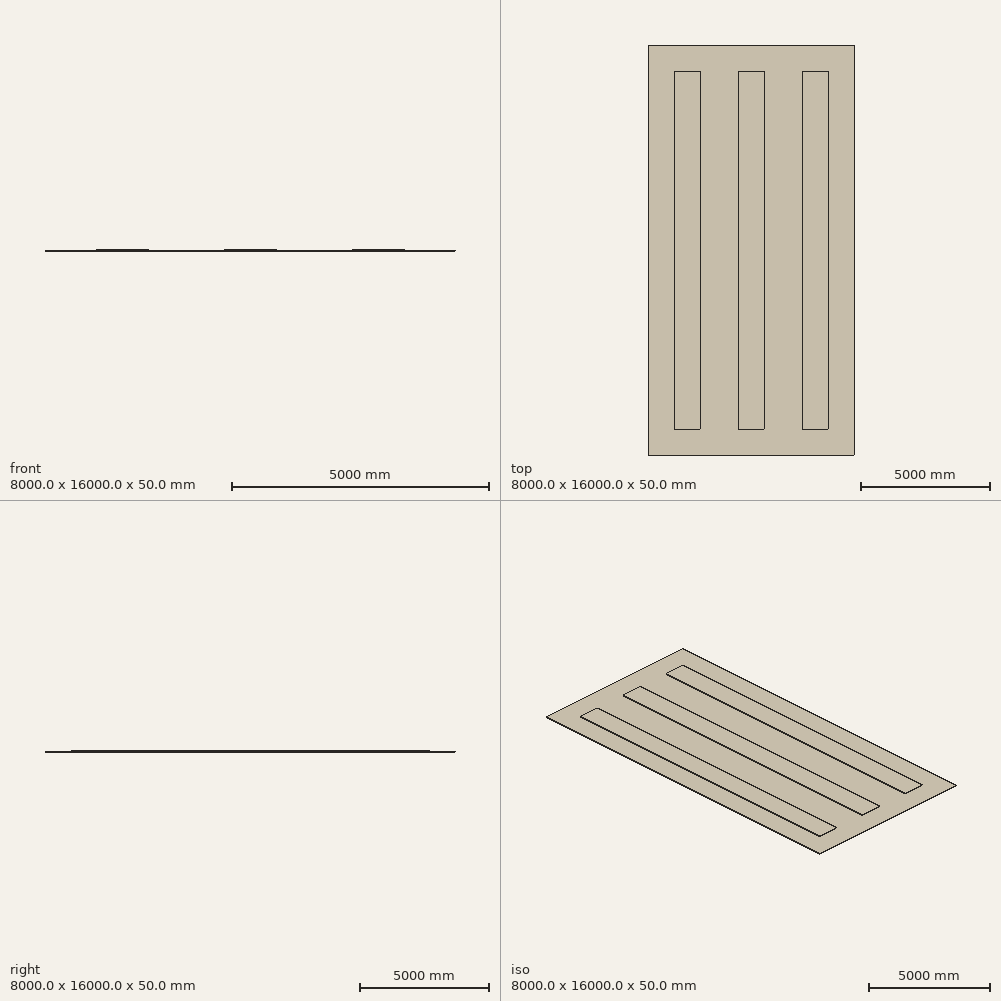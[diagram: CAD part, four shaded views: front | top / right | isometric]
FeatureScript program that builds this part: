
annotation { "Feature Type Name" : "Feature", "Feature Type Description" : "" }
export const myFeature = defineFeature(function(context is Context, id is Id, definition is map)
    precondition{}
    {
        {
            var Q0;
            Q0=qCreatedBy(makeId("Top.planeOp"),FACE);
            var sketch = newSketch(context, id + "F0", { "sketchPlane" : qUnion([Q0])});
            skLineSegment(sketch, "E0.bottom", {"start": v(0, 0) * mm, "end": v(-8000, 0) * mm});
            skLineSegment(sketch, "E0.top", {"start": v(0, 16000) * mm, "end": v(-8000, 16000) * mm});
            skLineSegment(sketch, "E0.left", {"start": v(0, 0) * mm, "end": v(0, 16000) * mm});
            skLineSegment(sketch, "E0.right", {"start": v(-8000, 0) * mm, "end": v(-8000, 16000) * mm});
            skSolve(sketch);
        }
        {
            var Q0;
            Q0=makeQuery(id+"F0.imprint","IMPRINT",FACE,{"disambiguationData":[TD([[makeQuery(id+"F0.imprint","IMPRINT",EDGE,{"derivedFrom":sQuery(id+"F0.wireOp",EDGE,"E0.bottom")}),-1.0]])]});
            extrude(context, id + "F1", {"entities" : qUnion([Q0]), "depth" : 25 * mm, "offsetDistance" : 25 * mm});
        }
        {
            var Q0;
            Q0=makeQuery(id+"F1.opExtrude","CAP_FACE",FACE,{"disambiguationData":[OSD([sQuery(id+"F0.wireOp",EDGE,"E0.bottom"),sQuery(id+"F0.wireOp",EDGE,"E0.top"),sQuery(id+"F0.wireOp",EDGE,"E0.left"),sQuery(id+"F0.wireOp",EDGE,"E0.right")])],"isStart":false});
            var sketch = newSketch(context, id + "F2", { "sketchPlane" : qUnion([Q0])});
            skLineSegment(sketch, "E1", {"start": v(-8000, 0) * mm, "end": v(-7000, 0) * mm});
            skLineSegment(sketch, "E2", {"start": v(-7000, 0) * mm, "end": v(-6000, 0) * mm});
            skLineSegment(sketch, "E3", {"start": v(-6000, 0) * mm, "end": v(-4500, 0) * mm});
            skLineSegment(sketch, "E4", {"start": v(-4500, 0) * mm, "end": v(-3500, 0) * mm});
            skLineSegment(sketch, "E5", {"start": v(-3500, 0) * mm, "end": v(-2000, 0) * mm});
            skLineSegment(sketch, "E6", {"start": v(-2000, 0) * mm, "end": v(-1000, 0) * mm});
            skLineSegment(sketch, "E7", {"start": v(-1000, 0) * mm, "end": v(0, 0) * mm});
            skLineSegment(sketch, "E8", {"start": v(-8000, 0) * mm, "end": v(-8000, 1000) * mm});
            skLineSegment(sketch, "E9", {"start": v(-8000, 1000) * mm, "end": v(-8000, 2000) * mm});
            skLineSegment(sketch, "E10", {"start": v(-8000, 2000) * mm, "end": v(-8000, 3000) * mm});
            skLineSegment(sketch, "E11", {"start": v(-8000, 3000) * mm, "end": v(-8000, 4000) * mm});
            skLineSegment(sketch, "E12", {"start": v(-8000, 4000) * mm, "end": v(-8000, 5000) * mm});
            skLineSegment(sketch, "E13", {"start": v(-8000, 5000) * mm, "end": v(-8000, 6000) * mm});
            skLineSegment(sketch, "E14", {"start": v(-8000, 6000) * mm, "end": v(-8000, 7000) * mm});
            skLineSegment(sketch, "E15", {"start": v(-8000, 7000) * mm, "end": v(-8000, 8000) * mm});
            skLineSegment(sketch, "E16", {"start": v(-8000, 8000) * mm, "end": v(-8000, 9000) * mm});
            skLineSegment(sketch, "E17", {"start": v(-8000, 9000) * mm, "end": v(-8000, 10000) * mm});
            skLineSegment(sketch, "E18", {"start": v(-8000, 10000) * mm, "end": v(-8000, 11000) * mm});
            skLineSegment(sketch, "E19", {"start": v(-8000, 11000) * mm, "end": v(-8000, 12000) * mm});
            skLineSegment(sketch, "E20", {"start": v(-8000, 12000) * mm, "end": v(-8000, 13000) * mm});
            skLineSegment(sketch, "E21", {"start": v(-8000, 13000) * mm, "end": v(-8000, 14000) * mm});
            skLineSegment(sketch, "E22", {"start": v(-8000, 14000) * mm, "end": v(-8000, 15000) * mm});
            skLineSegment(sketch, "E23", {"start": v(-8000, 15000) * mm, "end": v(-8000, 16000) * mm});
            skLineSegment(sketch, "E24", {"start": v(-8000, 16000) * mm, "end": v(-8000, 15000) * mm});
            skLineSegment(sketch, "E25", {"start": v(-8000, 1000) * mm, "end": v(0, 1000) * mm});
            skLineSegment(sketch, "E26", {"start": v(-8000, 2000) * mm, "end": v(0, 2000) * mm});
            skLineSegment(sketch, "E27", {"start": v(-8000, 3000) * mm, "end": v(0, 3000) * mm});
            skLineSegment(sketch, "E28", {"start": v(-8000, 4000) * mm, "end": v(0, 4000) * mm});
            skLineSegment(sketch, "E29", {"start": v(-8000, 5000) * mm, "end": v(0, 5000) * mm});
            skLineSegment(sketch, "E30", {"start": v(-8000, 6000) * mm, "end": v(0, 6000) * mm});
            skLineSegment(sketch, "E31", {"start": v(-8000, 7000) * mm, "end": v(0, 7000) * mm});
            skLineSegment(sketch, "E32", {"start": v(-8000, 8000) * mm, "end": v(0, 8000) * mm});
            skLineSegment(sketch, "E33", {"start": v(-8000, 9000) * mm, "end": v(0, 9000) * mm});
            skLineSegment(sketch, "E34", {"start": v(-8000, 10000) * mm, "end": v(0, 10000) * mm});
            skLineSegment(sketch, "E35", {"start": v(-8000, 11000) * mm, "end": v(0, 11000) * mm});
            skLineSegment(sketch, "E36", {"start": v(-8000, 12000) * mm, "end": v(0, 12000) * mm});
            skLineSegment(sketch, "E37", {"start": v(-8000, 13000) * mm, "end": v(0, 13000) * mm});
            skLineSegment(sketch, "E38", {"start": v(-8000, 14000) * mm, "end": v(0, 14000) * mm});
            skLineSegment(sketch, "E39", {"start": v(-8000, 15000) * mm, "end": v(0, 15000) * mm});
            skLineSegment(sketch, "E40", {"start": v(-1000, 0) * mm, "end": v(-1000, 16000) * mm});
            skLineSegment(sketch, "E41", {"start": v(-2000, 0) * mm, "end": v(-2000, 16000) * mm});
            skLineSegment(sketch, "E42", {"start": v(-3500, 0) * mm, "end": v(-3500, 16000) * mm});
            skLineSegment(sketch, "E43", {"start": v(-4500, 0) * mm, "end": v(-4500, 16000) * mm});
            skLineSegment(sketch, "E44", {"start": v(-6000, 0) * mm, "end": v(-6000, 16000) * mm});
            skLineSegment(sketch, "E45", {"start": v(-7000, 0) * mm, "end": v(-7000, 16000) * mm});
            skSolve(sketch);
        }
        {
            var Q0;
            {var subQ0=sQuery(id+"F2.wireOp",EDGE,"E45");var subQ1=sQuery(id+"F2.wireOp",EDGE,"E25");var subQ2=makeQuery(id+"F2.imprint","INTERSECT",VERTEX,{"derivedFrom":[subQ1,subQ0]});Q0=makeQuery(id+"F2.imprint","IMPRINT",FACE,{"disambiguationData":[TD([[makeQuery(id+"F2.imprint","IMPRINT",EDGE,{"disambiguationData":[TD([[subQ2,-1.0]])],"derivedFrom":subQ1}),1.0]])]});}
            var Q1;
            {var subQ0=sQuery(id+"F2.wireOp",EDGE,"E45");var subQ1=sQuery(id+"F2.wireOp",EDGE,"E26");var subQ2=makeQuery(id+"F2.imprint","INTERSECT",VERTEX,{"derivedFrom":[subQ1,subQ0]});Q1=makeQuery(id+"F2.imprint","IMPRINT",FACE,{"disambiguationData":[TD([[makeQuery(id+"F2.imprint","IMPRINT",EDGE,{"disambiguationData":[TD([[subQ2,-1.0]])],"derivedFrom":subQ1}),1.0]])]});}
            var Q2;
            {var subQ0=sQuery(id+"F2.wireOp",EDGE,"E45");var subQ1=sQuery(id+"F2.wireOp",EDGE,"E27");var subQ2=makeQuery(id+"F2.imprint","INTERSECT",VERTEX,{"derivedFrom":[subQ1,subQ0]});Q2=makeQuery(id+"F2.imprint","IMPRINT",FACE,{"disambiguationData":[TD([[makeQuery(id+"F2.imprint","IMPRINT",EDGE,{"disambiguationData":[TD([[subQ2,-1.0]])],"derivedFrom":subQ1}),1.0]])]});}
            var Q3;
            {var subQ0=sQuery(id+"F2.wireOp",EDGE,"E45");var subQ1=sQuery(id+"F2.wireOp",EDGE,"E28");var subQ2=makeQuery(id+"F2.imprint","INTERSECT",VERTEX,{"derivedFrom":[subQ1,subQ0]});Q3=makeQuery(id+"F2.imprint","IMPRINT",FACE,{"disambiguationData":[TD([[makeQuery(id+"F2.imprint","IMPRINT",EDGE,{"disambiguationData":[TD([[subQ2,-1.0]])],"derivedFrom":subQ1}),1.0]])]});}
            var Q4;
            {var subQ0=sQuery(id+"F2.wireOp",EDGE,"E45");var subQ1=sQuery(id+"F2.wireOp",EDGE,"E29");var subQ2=makeQuery(id+"F2.imprint","INTERSECT",VERTEX,{"derivedFrom":[subQ1,subQ0]});Q4=makeQuery(id+"F2.imprint","IMPRINT",FACE,{"disambiguationData":[TD([[makeQuery(id+"F2.imprint","IMPRINT",EDGE,{"disambiguationData":[TD([[subQ2,-1.0]])],"derivedFrom":subQ1}),1.0]])]});}
            var Q5;
            {var subQ0=sQuery(id+"F2.wireOp",EDGE,"E45");var subQ1=sQuery(id+"F2.wireOp",EDGE,"E30");var subQ2=makeQuery(id+"F2.imprint","INTERSECT",VERTEX,{"derivedFrom":[subQ1,subQ0]});Q5=makeQuery(id+"F2.imprint","IMPRINT",FACE,{"disambiguationData":[TD([[makeQuery(id+"F2.imprint","IMPRINT",EDGE,{"disambiguationData":[TD([[subQ2,-1.0]])],"derivedFrom":subQ1}),1.0]])]});}
            var Q6;
            {var subQ0=sQuery(id+"F2.wireOp",EDGE,"E45");var subQ1=sQuery(id+"F2.wireOp",EDGE,"E31");var subQ2=makeQuery(id+"F2.imprint","INTERSECT",VERTEX,{"derivedFrom":[subQ1,subQ0]});Q6=makeQuery(id+"F2.imprint","IMPRINT",FACE,{"disambiguationData":[TD([[makeQuery(id+"F2.imprint","IMPRINT",EDGE,{"disambiguationData":[TD([[subQ2,-1.0]])],"derivedFrom":subQ1}),1.0]])]});}
            var Q7;
            {var subQ0=sQuery(id+"F2.wireOp",EDGE,"E45");var subQ1=sQuery(id+"F2.wireOp",EDGE,"E32");var subQ2=makeQuery(id+"F2.imprint","INTERSECT",VERTEX,{"derivedFrom":[subQ1,subQ0]});Q7=makeQuery(id+"F2.imprint","IMPRINT",FACE,{"disambiguationData":[TD([[makeQuery(id+"F2.imprint","IMPRINT",EDGE,{"disambiguationData":[TD([[subQ2,-1.0]])],"derivedFrom":subQ1}),1.0]])]});}
            var Q8;
            {var subQ0=sQuery(id+"F2.wireOp",EDGE,"E45");var subQ1=sQuery(id+"F2.wireOp",EDGE,"E33");var subQ2=makeQuery(id+"F2.imprint","INTERSECT",VERTEX,{"derivedFrom":[subQ1,subQ0]});Q8=makeQuery(id+"F2.imprint","IMPRINT",FACE,{"disambiguationData":[TD([[makeQuery(id+"F2.imprint","IMPRINT",EDGE,{"disambiguationData":[TD([[subQ2,-1.0]])],"derivedFrom":subQ1}),1.0]])]});}
            var Q9;
            {var subQ0=sQuery(id+"F2.wireOp",EDGE,"E45");var subQ1=sQuery(id+"F2.wireOp",EDGE,"E34");var subQ2=makeQuery(id+"F2.imprint","INTERSECT",VERTEX,{"derivedFrom":[subQ1,subQ0]});Q9=makeQuery(id+"F2.imprint","IMPRINT",FACE,{"disambiguationData":[TD([[makeQuery(id+"F2.imprint","IMPRINT",EDGE,{"disambiguationData":[TD([[subQ2,-1.0]])],"derivedFrom":subQ1}),1.0]])]});}
            var Q10;
            {var subQ0=sQuery(id+"F2.wireOp",EDGE,"E45");var subQ1=sQuery(id+"F2.wireOp",EDGE,"E35");var subQ2=makeQuery(id+"F2.imprint","INTERSECT",VERTEX,{"derivedFrom":[subQ1,subQ0]});Q10=makeQuery(id+"F2.imprint","IMPRINT",FACE,{"disambiguationData":[TD([[makeQuery(id+"F2.imprint","IMPRINT",EDGE,{"disambiguationData":[TD([[subQ2,-1.0]])],"derivedFrom":subQ1}),1.0]])]});}
            var Q11;
            {var subQ0=sQuery(id+"F2.wireOp",EDGE,"E45");var subQ1=sQuery(id+"F2.wireOp",EDGE,"E36");var subQ2=makeQuery(id+"F2.imprint","INTERSECT",VERTEX,{"derivedFrom":[subQ1,subQ0]});Q11=makeQuery(id+"F2.imprint","IMPRINT",FACE,{"disambiguationData":[TD([[makeQuery(id+"F2.imprint","IMPRINT",EDGE,{"disambiguationData":[TD([[subQ2,-1.0]])],"derivedFrom":subQ1}),1.0]])]});}
            var Q12;
            {var subQ0=sQuery(id+"F2.wireOp",EDGE,"E45");var subQ1=sQuery(id+"F2.wireOp",EDGE,"E37");var subQ2=makeQuery(id+"F2.imprint","INTERSECT",VERTEX,{"derivedFrom":[subQ1,subQ0]});Q12=makeQuery(id+"F2.imprint","IMPRINT",FACE,{"disambiguationData":[TD([[makeQuery(id+"F2.imprint","IMPRINT",EDGE,{"disambiguationData":[TD([[subQ2,-1.0]])],"derivedFrom":subQ1}),1.0]])]});}
            var Q13;
            {var subQ0=sQuery(id+"F2.wireOp",EDGE,"E45");var subQ1=sQuery(id+"F2.wireOp",EDGE,"E38");var subQ2=makeQuery(id+"F2.imprint","INTERSECT",VERTEX,{"derivedFrom":[subQ1,subQ0]});Q13=makeQuery(id+"F2.imprint","IMPRINT",FACE,{"disambiguationData":[TD([[makeQuery(id+"F2.imprint","IMPRINT",EDGE,{"disambiguationData":[TD([[subQ2,-1.0]])],"derivedFrom":subQ1}),1.0]])]});}
            var Q14;
            {var subQ0=sQuery(id+"F2.wireOp",EDGE,"E43");var subQ1=sQuery(id+"F2.wireOp",EDGE,"E38");var subQ2=makeQuery(id+"F2.imprint","INTERSECT",VERTEX,{"derivedFrom":[subQ1,subQ0]});Q14=makeQuery(id+"F2.imprint","IMPRINT",FACE,{"disambiguationData":[TD([[makeQuery(id+"F2.imprint","IMPRINT",EDGE,{"disambiguationData":[TD([[subQ2,-1.0]])],"derivedFrom":subQ1}),1.0]])]});}
            var Q15;
            {var subQ0=sQuery(id+"F2.wireOp",EDGE,"E43");var subQ1=sQuery(id+"F2.wireOp",EDGE,"E37");var subQ2=makeQuery(id+"F2.imprint","INTERSECT",VERTEX,{"derivedFrom":[subQ1,subQ0]});Q15=makeQuery(id+"F2.imprint","IMPRINT",FACE,{"disambiguationData":[TD([[makeQuery(id+"F2.imprint","IMPRINT",EDGE,{"disambiguationData":[TD([[subQ2,-1.0]])],"derivedFrom":subQ1}),1.0]])]});}
            var Q16;
            {var subQ0=sQuery(id+"F2.wireOp",EDGE,"E43");var subQ1=sQuery(id+"F2.wireOp",EDGE,"E36");var subQ2=makeQuery(id+"F2.imprint","INTERSECT",VERTEX,{"derivedFrom":[subQ1,subQ0]});Q16=makeQuery(id+"F2.imprint","IMPRINT",FACE,{"disambiguationData":[TD([[makeQuery(id+"F2.imprint","IMPRINT",EDGE,{"disambiguationData":[TD([[subQ2,-1.0]])],"derivedFrom":subQ1}),1.0]])]});}
            var Q17;
            {var subQ0=sQuery(id+"F2.wireOp",EDGE,"E43");var subQ1=sQuery(id+"F2.wireOp",EDGE,"E35");var subQ2=makeQuery(id+"F2.imprint","INTERSECT",VERTEX,{"derivedFrom":[subQ1,subQ0]});Q17=makeQuery(id+"F2.imprint","IMPRINT",FACE,{"disambiguationData":[TD([[makeQuery(id+"F2.imprint","IMPRINT",EDGE,{"disambiguationData":[TD([[subQ2,-1.0]])],"derivedFrom":subQ1}),1.0]])]});}
            var Q18;
            {var subQ0=sQuery(id+"F2.wireOp",EDGE,"E43");var subQ1=sQuery(id+"F2.wireOp",EDGE,"E34");var subQ2=makeQuery(id+"F2.imprint","INTERSECT",VERTEX,{"derivedFrom":[subQ1,subQ0]});Q18=makeQuery(id+"F2.imprint","IMPRINT",FACE,{"disambiguationData":[TD([[makeQuery(id+"F2.imprint","IMPRINT",EDGE,{"disambiguationData":[TD([[subQ2,-1.0]])],"derivedFrom":subQ1}),1.0]])]});}
            var Q19;
            {var subQ0=sQuery(id+"F2.wireOp",EDGE,"E43");var subQ1=sQuery(id+"F2.wireOp",EDGE,"E33");var subQ2=makeQuery(id+"F2.imprint","INTERSECT",VERTEX,{"derivedFrom":[subQ1,subQ0]});Q19=makeQuery(id+"F2.imprint","IMPRINT",FACE,{"disambiguationData":[TD([[makeQuery(id+"F2.imprint","IMPRINT",EDGE,{"disambiguationData":[TD([[subQ2,-1.0]])],"derivedFrom":subQ1}),1.0]])]});}
            var Q20;
            {var subQ0=sQuery(id+"F2.wireOp",EDGE,"E43");var subQ1=sQuery(id+"F2.wireOp",EDGE,"E32");var subQ2=makeQuery(id+"F2.imprint","INTERSECT",VERTEX,{"derivedFrom":[subQ1,subQ0]});Q20=makeQuery(id+"F2.imprint","IMPRINT",FACE,{"disambiguationData":[TD([[makeQuery(id+"F2.imprint","IMPRINT",EDGE,{"disambiguationData":[TD([[subQ2,-1.0]])],"derivedFrom":subQ1}),1.0]])]});}
            var Q21;
            {var subQ0=sQuery(id+"F2.wireOp",EDGE,"E43");var subQ1=sQuery(id+"F2.wireOp",EDGE,"E31");var subQ2=makeQuery(id+"F2.imprint","INTERSECT",VERTEX,{"derivedFrom":[subQ1,subQ0]});Q21=makeQuery(id+"F2.imprint","IMPRINT",FACE,{"disambiguationData":[TD([[makeQuery(id+"F2.imprint","IMPRINT",EDGE,{"disambiguationData":[TD([[subQ2,-1.0]])],"derivedFrom":subQ1}),1.0]])]});}
            var Q22;
            {var subQ0=sQuery(id+"F2.wireOp",EDGE,"E43");var subQ1=sQuery(id+"F2.wireOp",EDGE,"E30");var subQ2=makeQuery(id+"F2.imprint","INTERSECT",VERTEX,{"derivedFrom":[subQ1,subQ0]});Q22=makeQuery(id+"F2.imprint","IMPRINT",FACE,{"disambiguationData":[TD([[makeQuery(id+"F2.imprint","IMPRINT",EDGE,{"disambiguationData":[TD([[subQ2,-1.0]])],"derivedFrom":subQ1}),1.0]])]});}
            var Q23;
            {var subQ0=sQuery(id+"F2.wireOp",EDGE,"E43");var subQ1=sQuery(id+"F2.wireOp",EDGE,"E29");var subQ2=makeQuery(id+"F2.imprint","INTERSECT",VERTEX,{"derivedFrom":[subQ1,subQ0]});Q23=makeQuery(id+"F2.imprint","IMPRINT",FACE,{"disambiguationData":[TD([[makeQuery(id+"F2.imprint","IMPRINT",EDGE,{"disambiguationData":[TD([[subQ2,-1.0]])],"derivedFrom":subQ1}),1.0]])]});}
            var Q24;
            {var subQ0=sQuery(id+"F2.wireOp",EDGE,"E43");var subQ1=sQuery(id+"F2.wireOp",EDGE,"E28");var subQ2=makeQuery(id+"F2.imprint","INTERSECT",VERTEX,{"derivedFrom":[subQ1,subQ0]});Q24=makeQuery(id+"F2.imprint","IMPRINT",FACE,{"disambiguationData":[TD([[makeQuery(id+"F2.imprint","IMPRINT",EDGE,{"disambiguationData":[TD([[subQ2,-1.0]])],"derivedFrom":subQ1}),1.0]])]});}
            var Q25;
            {var subQ0=sQuery(id+"F2.wireOp",EDGE,"E43");var subQ1=sQuery(id+"F2.wireOp",EDGE,"E27");var subQ2=makeQuery(id+"F2.imprint","INTERSECT",VERTEX,{"derivedFrom":[subQ1,subQ0]});Q25=makeQuery(id+"F2.imprint","IMPRINT",FACE,{"disambiguationData":[TD([[makeQuery(id+"F2.imprint","IMPRINT",EDGE,{"disambiguationData":[TD([[subQ2,-1.0]])],"derivedFrom":subQ1}),1.0]])]});}
            var Q26;
            {var subQ0=sQuery(id+"F2.wireOp",EDGE,"E43");var subQ1=sQuery(id+"F2.wireOp",EDGE,"E26");var subQ2=makeQuery(id+"F2.imprint","INTERSECT",VERTEX,{"derivedFrom":[subQ1,subQ0]});Q26=makeQuery(id+"F2.imprint","IMPRINT",FACE,{"disambiguationData":[TD([[makeQuery(id+"F2.imprint","IMPRINT",EDGE,{"disambiguationData":[TD([[subQ2,-1.0]])],"derivedFrom":subQ1}),1.0]])]});}
            var Q27;
            {var subQ0=sQuery(id+"F2.wireOp",EDGE,"E43");var subQ1=sQuery(id+"F2.wireOp",EDGE,"E25");var subQ2=makeQuery(id+"F2.imprint","INTERSECT",VERTEX,{"derivedFrom":[subQ1,subQ0]});Q27=makeQuery(id+"F2.imprint","IMPRINT",FACE,{"disambiguationData":[TD([[makeQuery(id+"F2.imprint","IMPRINT",EDGE,{"disambiguationData":[TD([[subQ2,-1.0]])],"derivedFrom":subQ1}),1.0]])]});}
            var Q28;
            {var subQ0=sQuery(id+"F2.wireOp",EDGE,"E41");var subQ1=sQuery(id+"F2.wireOp",EDGE,"E25");var subQ2=makeQuery(id+"F2.imprint","INTERSECT",VERTEX,{"derivedFrom":[subQ1,subQ0]});Q28=makeQuery(id+"F2.imprint","IMPRINT",FACE,{"disambiguationData":[TD([[makeQuery(id+"F2.imprint","IMPRINT",EDGE,{"disambiguationData":[TD([[subQ2,-1.0]])],"derivedFrom":subQ1}),1.0]])]});}
            var Q29;
            {var subQ0=sQuery(id+"F2.wireOp",EDGE,"E41");var subQ1=sQuery(id+"F2.wireOp",EDGE,"E26");var subQ2=makeQuery(id+"F2.imprint","INTERSECT",VERTEX,{"derivedFrom":[subQ1,subQ0]});Q29=makeQuery(id+"F2.imprint","IMPRINT",FACE,{"disambiguationData":[TD([[makeQuery(id+"F2.imprint","IMPRINT",EDGE,{"disambiguationData":[TD([[subQ2,-1.0]])],"derivedFrom":subQ1}),1.0]])]});}
            var Q30;
            {var subQ0=sQuery(id+"F2.wireOp",EDGE,"E41");var subQ1=sQuery(id+"F2.wireOp",EDGE,"E27");var subQ2=makeQuery(id+"F2.imprint","INTERSECT",VERTEX,{"derivedFrom":[subQ1,subQ0]});Q30=makeQuery(id+"F2.imprint","IMPRINT",FACE,{"disambiguationData":[TD([[makeQuery(id+"F2.imprint","IMPRINT",EDGE,{"disambiguationData":[TD([[subQ2,-1.0]])],"derivedFrom":subQ1}),1.0]])]});}
            var Q31;
            {var subQ0=sQuery(id+"F2.wireOp",EDGE,"E41");var subQ1=sQuery(id+"F2.wireOp",EDGE,"E28");var subQ2=makeQuery(id+"F2.imprint","INTERSECT",VERTEX,{"derivedFrom":[subQ1,subQ0]});Q31=makeQuery(id+"F2.imprint","IMPRINT",FACE,{"disambiguationData":[TD([[makeQuery(id+"F2.imprint","IMPRINT",EDGE,{"disambiguationData":[TD([[subQ2,-1.0]])],"derivedFrom":subQ1}),1.0]])]});}
            var Q32;
            {var subQ0=sQuery(id+"F2.wireOp",EDGE,"E41");var subQ1=sQuery(id+"F2.wireOp",EDGE,"E29");var subQ2=makeQuery(id+"F2.imprint","INTERSECT",VERTEX,{"derivedFrom":[subQ1,subQ0]});Q32=makeQuery(id+"F2.imprint","IMPRINT",FACE,{"disambiguationData":[TD([[makeQuery(id+"F2.imprint","IMPRINT",EDGE,{"disambiguationData":[TD([[subQ2,-1.0]])],"derivedFrom":subQ1}),1.0]])]});}
            var Q33;
            {var subQ0=sQuery(id+"F2.wireOp",EDGE,"E41");var subQ1=sQuery(id+"F2.wireOp",EDGE,"E30");var subQ2=makeQuery(id+"F2.imprint","INTERSECT",VERTEX,{"derivedFrom":[subQ1,subQ0]});Q33=makeQuery(id+"F2.imprint","IMPRINT",FACE,{"disambiguationData":[TD([[makeQuery(id+"F2.imprint","IMPRINT",EDGE,{"disambiguationData":[TD([[subQ2,-1.0]])],"derivedFrom":subQ1}),1.0]])]});}
            var Q34;
            {var subQ0=sQuery(id+"F2.wireOp",EDGE,"E41");var subQ1=sQuery(id+"F2.wireOp",EDGE,"E31");var subQ2=makeQuery(id+"F2.imprint","INTERSECT",VERTEX,{"derivedFrom":[subQ1,subQ0]});Q34=makeQuery(id+"F2.imprint","IMPRINT",FACE,{"disambiguationData":[TD([[makeQuery(id+"F2.imprint","IMPRINT",EDGE,{"disambiguationData":[TD([[subQ2,-1.0]])],"derivedFrom":subQ1}),1.0]])]});}
            var Q35;
            {var subQ0=sQuery(id+"F2.wireOp",EDGE,"E41");var subQ1=sQuery(id+"F2.wireOp",EDGE,"E32");var subQ2=makeQuery(id+"F2.imprint","INTERSECT",VERTEX,{"derivedFrom":[subQ1,subQ0]});Q35=makeQuery(id+"F2.imprint","IMPRINT",FACE,{"disambiguationData":[TD([[makeQuery(id+"F2.imprint","IMPRINT",EDGE,{"disambiguationData":[TD([[subQ2,-1.0]])],"derivedFrom":subQ1}),1.0]])]});}
            var Q36;
            {var subQ0=sQuery(id+"F2.wireOp",EDGE,"E41");var subQ1=sQuery(id+"F2.wireOp",EDGE,"E33");var subQ2=makeQuery(id+"F2.imprint","INTERSECT",VERTEX,{"derivedFrom":[subQ1,subQ0]});Q36=makeQuery(id+"F2.imprint","IMPRINT",FACE,{"disambiguationData":[TD([[makeQuery(id+"F2.imprint","IMPRINT",EDGE,{"disambiguationData":[TD([[subQ2,-1.0]])],"derivedFrom":subQ1}),1.0]])]});}
            var Q37;
            {var subQ0=sQuery(id+"F2.wireOp",EDGE,"E41");var subQ1=sQuery(id+"F2.wireOp",EDGE,"E34");var subQ2=makeQuery(id+"F2.imprint","INTERSECT",VERTEX,{"derivedFrom":[subQ1,subQ0]});Q37=makeQuery(id+"F2.imprint","IMPRINT",FACE,{"disambiguationData":[TD([[makeQuery(id+"F2.imprint","IMPRINT",EDGE,{"disambiguationData":[TD([[subQ2,-1.0]])],"derivedFrom":subQ1}),1.0]])]});}
            var Q38;
            {var subQ0=sQuery(id+"F2.wireOp",EDGE,"E41");var subQ1=sQuery(id+"F2.wireOp",EDGE,"E35");var subQ2=makeQuery(id+"F2.imprint","INTERSECT",VERTEX,{"derivedFrom":[subQ1,subQ0]});Q38=makeQuery(id+"F2.imprint","IMPRINT",FACE,{"disambiguationData":[TD([[makeQuery(id+"F2.imprint","IMPRINT",EDGE,{"disambiguationData":[TD([[subQ2,-1.0]])],"derivedFrom":subQ1}),1.0]])]});}
            var Q39;
            {var subQ0=sQuery(id+"F2.wireOp",EDGE,"E41");var subQ1=sQuery(id+"F2.wireOp",EDGE,"E36");var subQ2=makeQuery(id+"F2.imprint","INTERSECT",VERTEX,{"derivedFrom":[subQ1,subQ0]});Q39=makeQuery(id+"F2.imprint","IMPRINT",FACE,{"disambiguationData":[TD([[makeQuery(id+"F2.imprint","IMPRINT",EDGE,{"disambiguationData":[TD([[subQ2,-1.0]])],"derivedFrom":subQ1}),1.0]])]});}
            var Q40;
            {var subQ0=sQuery(id+"F2.wireOp",EDGE,"E41");var subQ1=sQuery(id+"F2.wireOp",EDGE,"E37");var subQ2=makeQuery(id+"F2.imprint","INTERSECT",VERTEX,{"derivedFrom":[subQ1,subQ0]});Q40=makeQuery(id+"F2.imprint","IMPRINT",FACE,{"disambiguationData":[TD([[makeQuery(id+"F2.imprint","IMPRINT",EDGE,{"disambiguationData":[TD([[subQ2,-1.0]])],"derivedFrom":subQ1}),1.0]])]});}
            var Q41;
            {var subQ0=sQuery(id+"F2.wireOp",EDGE,"E41");var subQ1=sQuery(id+"F2.wireOp",EDGE,"E38");var subQ2=makeQuery(id+"F2.imprint","INTERSECT",VERTEX,{"derivedFrom":[subQ1,subQ0]});Q41=makeQuery(id+"F2.imprint","IMPRINT",FACE,{"disambiguationData":[TD([[makeQuery(id+"F2.imprint","IMPRINT",EDGE,{"disambiguationData":[TD([[subQ2,-1.0]])],"derivedFrom":subQ1}),1.0]])]});}
            extrude(context, id + "F3", {"entities" : qUnion([Q0, Q1, Q2, Q3, Q4, Q5, Q6, Q7, Q8, Q9, Q10, Q11, Q12, Q13, Q14, Q15, Q16, Q17, Q18, Q19, Q20, Q21, Q22, Q23, Q24, Q25, Q26, Q27, Q28, Q29, Q30, Q31, Q32, Q33, Q34, Q35, Q36, Q37, Q38, Q39, Q40, Q41]), "operationType" : NewBodyOperationType.ADD, "depth" : 25 * mm, "offsetDistance" : 25 * mm});
        }
    });
